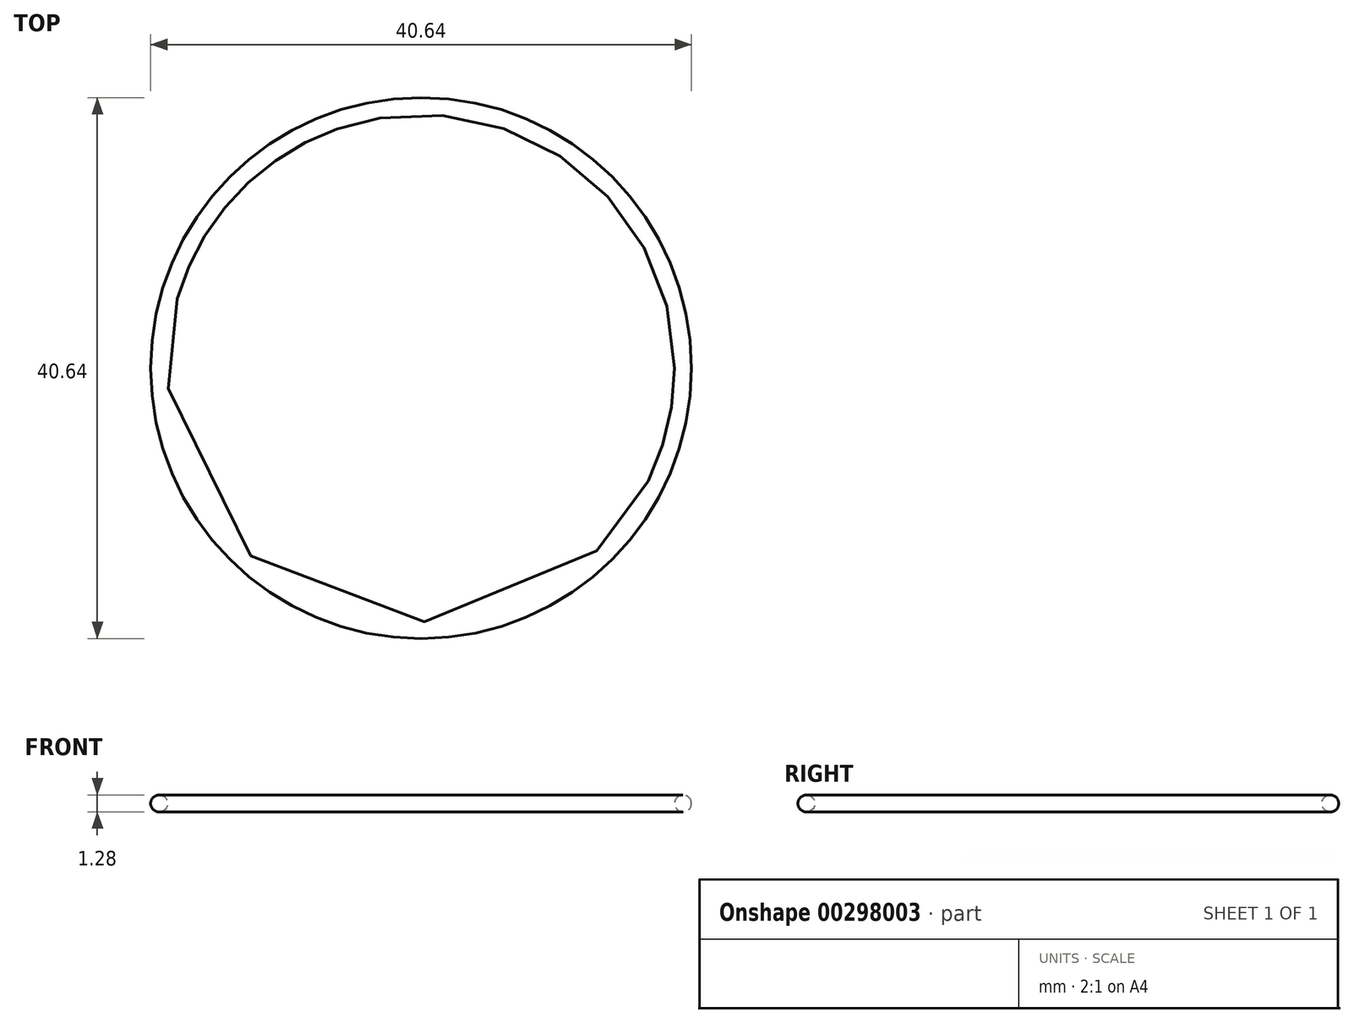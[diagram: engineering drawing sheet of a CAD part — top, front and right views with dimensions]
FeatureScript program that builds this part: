
annotation { "Feature Type Name" : "Feature", "Feature Type Description" : "" }
export const myFeature = defineFeature(function(context is Context, id is Id, definition is map)
    precondition{}
    {
        {
            var Q0;
            Q0=qCreatedBy(makeId("Top.planeOp"),FACE);
            var sketch = newSketch(context, id + "F0", { "sketchPlane" : qUnion([Q0])});
            skCircle(sketch, "E0", {"center": v(0, 0) * mm, "radius": 19.05 * mm});
            skSolve(sketch);
        }
        {
            var Q0;
            Q0=qCreatedBy(makeId("Front.planeOp"),FACE);
            var sketch = newSketch(context, id + "F1", { "sketchPlane" : qUnion([Q0])});
            skCircle(sketch, "E1", {"center": v(-19.69, 0) * mm, "radius": 0.64 * mm});
            skPoint(sketch, "E2", {"position": v(-19.05, 0) * mm});
            skSolve(sketch);
        }
        {
            var Q0;
            Q0=makeQuery(id+"F1.imprint","IMPRINT",FACE,{"disambiguationData":[TD([[makeQuery(id+"F1.imprint","IMPRINT",EDGE,{"derivedFrom":sQuery(id+"F1.wireOp",EDGE,"E1")}),1.0]])]});
            var Q1;
            Q1=sQuery(id+"F0.wireOp",EDGE,"E0");
            sweep(context, id + "F2", {"profiles" : qUnion([Q0]), "path" : qUnion([Q1])});
        }
    });
